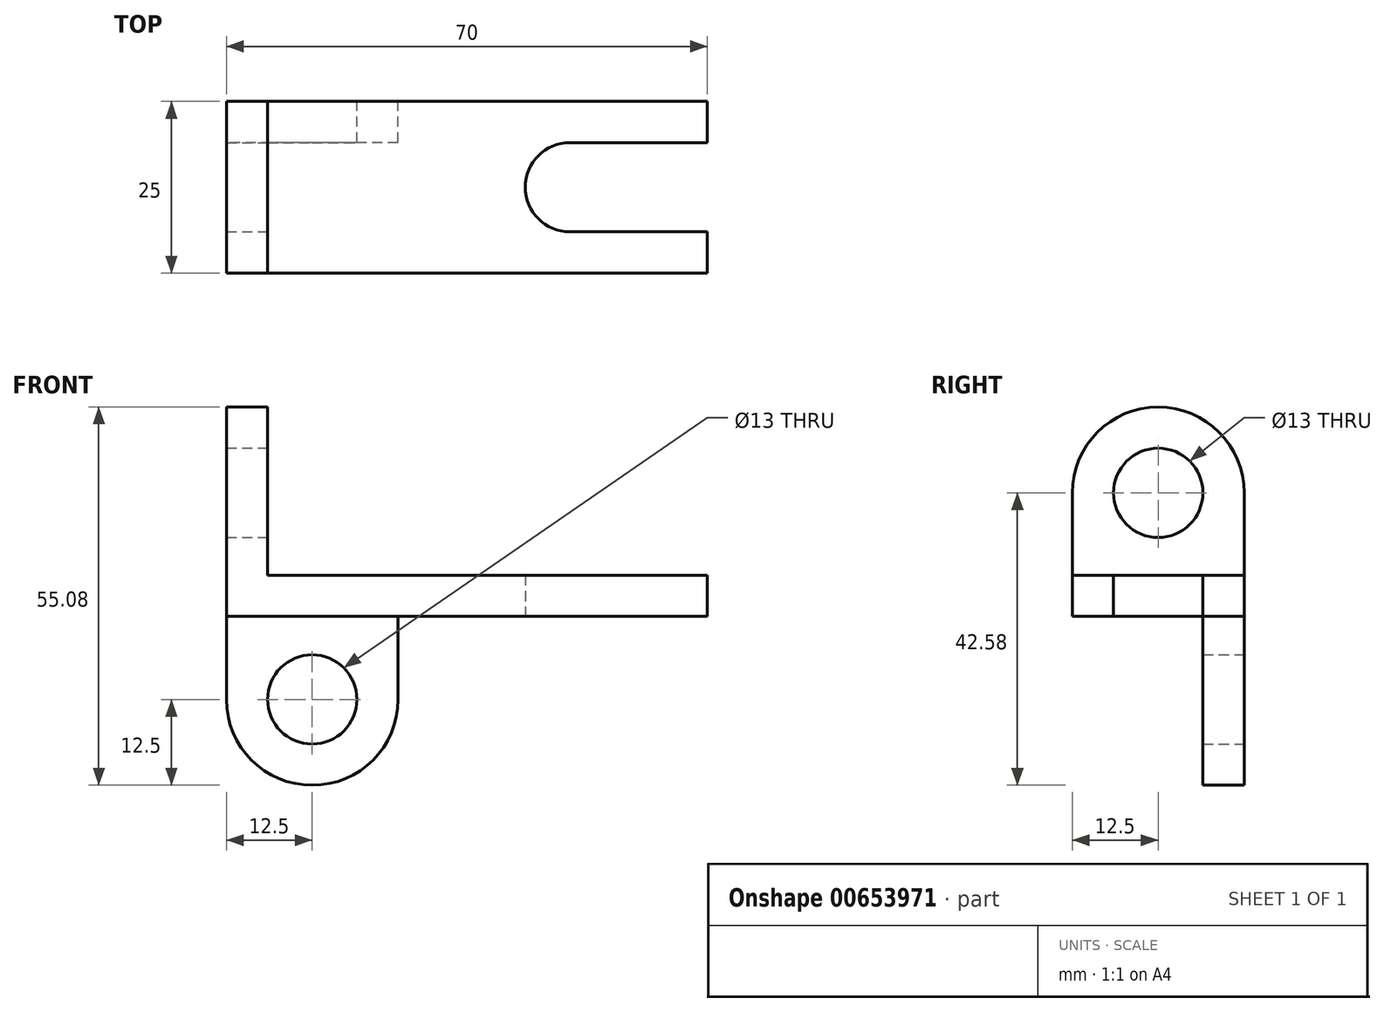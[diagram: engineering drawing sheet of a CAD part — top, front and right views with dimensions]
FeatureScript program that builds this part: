
annotation { "Feature Type Name" : "Feature", "Feature Type Description" : "" }
export const myFeature = defineFeature(function(context is Context, id is Id, definition is map)
    precondition{}
    {
        {
            var Q0;
            Q0=qCreatedBy(makeId("Top.planeOp"),FACE);
            var sketch = newSketch(context, id + "F0", { "sketchPlane" : qUnion([Q0])});
            skLineSegment(sketch, "E0.bottom", {"start": v(0, 0) * mm, "end": v(64, 0) * mm});
            skLineSegment(sketch, "E0.top", {"start": v(0, -25) * mm, "end": v(64, -25) * mm});
            skLineSegment(sketch, "E0.left", {"start": v(0, 0) * mm, "end": v(0, -25) * mm});
            skLineSegment(sketch, "E0.right", {"start": v(64, 0) * mm, "end": v(64, -25) * mm});
            skLineSegment(sketch, "E1.bottom", {"start": v(64, -19) * mm, "end": v(44, -19) * mm});
            skLineSegment(sketch, "E1.top", {"start": v(64, -6) * mm, "end": v(44, -6) * mm});
            skLineSegment(sketch, "E1.left", {"start": v(64, -19) * mm, "end": v(64, -6) * mm});
            skLineSegment(sketch, "E1.right", {"start": v(44, -19) * mm, "end": v(44, -6) * mm});
            skPoint(sketch, "E1.middle", {"position": v(54, -12.5) * mm});
            skPoint(sketch, "E1.middle.positionSnap0", {"position": v(64, -12.5) * mm});
            skPoint(sketch, "E1.centerSnap0", {"position": v(64, -12.5) * mm});
            skCircle(sketch, "E2", {"center": v(44, -12.5) * mm, "radius": 6.5 * mm});
            skSolve(sketch);
        }
        {
            var Q0;
            {var subQ1=sQuery(id+"F0.wireOp",EDGE,"E0.bottom");Q0=makeQuery(id+"F0.imprint","IMPRINT",FACE,{"disambiguationData":[TD([[makeQuery(id+"F0.imprint","IMPRINT",EDGE,{"derivedFrom":subQ1}),-1.0]])]});}
            extrude(context, id + "F1", {"entities" : qUnion([Q0]), "depth" : 6 * mm, "offsetDistance" : 25 * mm});
        }
        {
            var Q0;
            Q0=makeQuery(id+"F1.opExtrude","SWEPT_FACE",FACE,{"disambiguationData":[OSD([sQuery(id+"F0.wireOp",EDGE,"E0.left")])]});
            var sketch = newSketch(context, id + "F2", { "sketchPlane" : qUnion([Q0])});
            skLineSegment(sketch, "E3.bottom", {"start": v(25, 0) * mm, "end": v(0, 0) * mm});
            skLineSegment(sketch, "E3.top", {"start": v(25, 18) * mm, "end": v(0, 18) * mm});
            skLineSegment(sketch, "E3.left", {"start": v(25, 0) * mm, "end": v(25, 18) * mm});
            skLineSegment(sketch, "E3.right", {"start": v(0, 0) * mm, "end": v(0, 18) * mm});
            skCircle(sketch, "E4", {"center": v(12.5, 18) * mm, "radius": 12.5 * mm});
            skCircle(sketch, "E5", {"center": v(12.5, 18) * mm, "radius": 6.5 * mm});
            skSolve(sketch);
        }
        {
            var Q0;
            Q0 = qSketchRegion(id + "F2", true);
            extrude(context, id + "F3", {"entities" : qUnion([Q0]), "operationType" : NewBodyOperationType.ADD, "depth" : 6 * mm, "offsetDistance" : 25 * mm});
        }
        {
            var Q0;
            Q0=makeQuery(id+"F3.boolean.opBoolean","MERGE",FACE,{"derivedFrom":[makeQuery(id+"F1.opExtrude","SWEPT_FACE",FACE,{"disambiguationData":[OSD([sQuery(id+"F0.wireOp",EDGE,"E0.bottom")])]}),makeQuery(id+"F3.opExtrude","SWEPT_FACE",FACE,{"disambiguationData":[OSD([sQuery(id+"F2.wireOp",EDGE,"E3.right")])]})]});
            var sketch = newSketch(context, id + "F4", { "sketchPlane" : qUnion([Q0])});
            skLineSegment(sketch, "E6.bottom", {"start": v(6, 5.92) * mm, "end": v(-19, 5.92) * mm});
            skLineSegment(sketch, "E6.top", {"start": v(6, -12.08) * mm, "end": v(-19, -12.08) * mm});
            skLineSegment(sketch, "E6.left", {"start": v(6, 5.92) * mm, "end": v(6, -12.08) * mm});
            skLineSegment(sketch, "E6.right", {"start": v(-19, 5.92) * mm, "end": v(-19, -12.08) * mm});
            skCircle(sketch, "E7", {"center": v(-6.5, -12.08) * mm, "radius": 12.5 * mm});
            skCircle(sketch, "E8", {"center": v(-6.5, -12.08) * mm, "radius": 6.5 * mm});
            skSolve(sketch);
        }
        {
            var Q0;
            Q0 = qSketchRegion(id + "F4", true);
            extrude(context, id + "F5", {"entities" : qUnion([Q0]), "operationType" : NewBodyOperationType.ADD, "oppositeDirection" : true, "depth" : 6 * mm, "offsetDistance" : 25 * mm});
        }
    });
